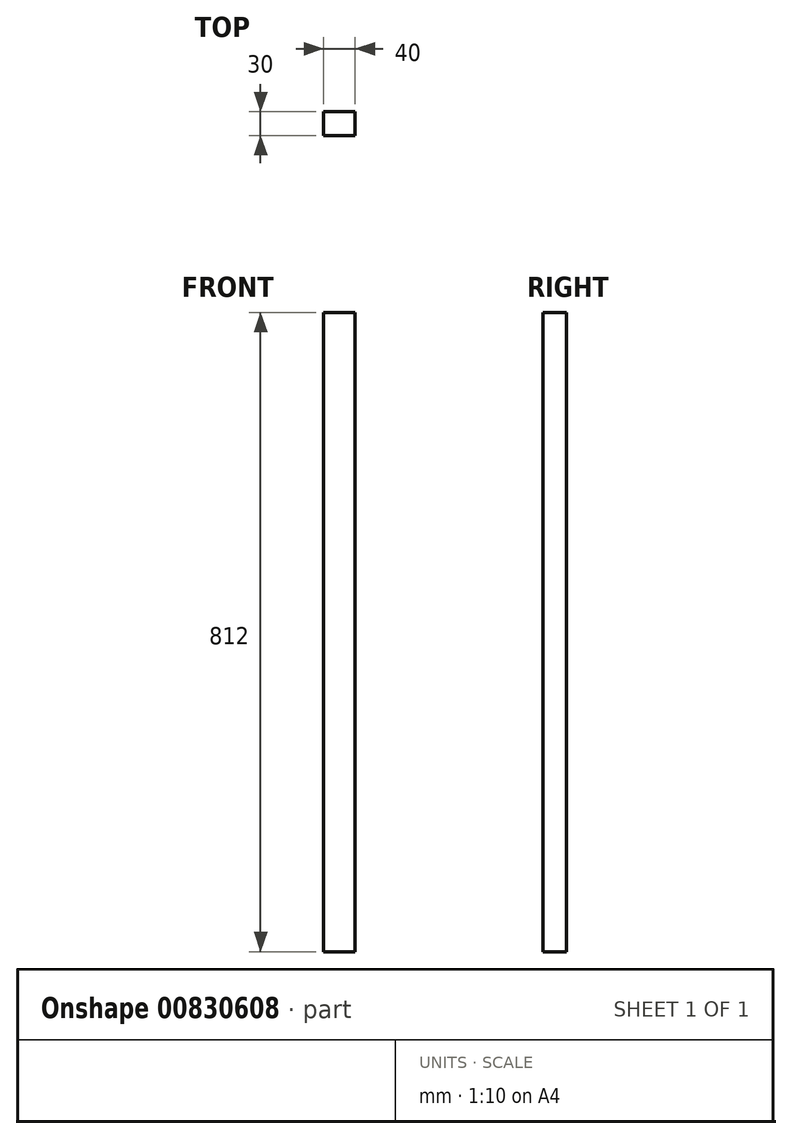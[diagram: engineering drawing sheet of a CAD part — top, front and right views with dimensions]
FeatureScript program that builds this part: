
annotation { "Feature Type Name" : "Feature", "Feature Type Description" : "" }
export const myFeature = defineFeature(function(context is Context, id is Id, definition is map)
    precondition{}
    {
        {
            var Q0;
            Q0=qCreatedBy(makeId("Top.planeOp"),FACE);
            var sketch = newSketch(context, id + "F0", { "sketchPlane" : qUnion([Q0])});
            skLineSegment(sketch, "E0.bottom", {"start": v(3.01, 0) * mm, "end": v(43.01, 0) * mm});
            skLineSegment(sketch, "E0.top", {"start": v(3.01, 30) * mm, "end": v(43.01, 30) * mm});
            skLineSegment(sketch, "E0.left", {"start": v(3.01, 0) * mm, "end": v(3.01, 30) * mm});
            skLineSegment(sketch, "E0.right", {"start": v(43.01, 0) * mm, "end": v(43.01, 30) * mm});
            skSolve(sketch);
        }
        {
            var Q0;
            Q0=makeQuery(id+"F0.imprint","IMPRINT",FACE,{"disambiguationData":[TD([[makeQuery(id+"F0.imprint","IMPRINT",EDGE,{"derivedFrom":sQuery(id+"F0.wireOp",EDGE,"E0.bottom")}),1.0]])]});
            extrude(context, id + "F1", {"entities" : qUnion([Q0]), "depth" : 812 * mm, "offsetDistance" : 25 * mm});
        }
    });
